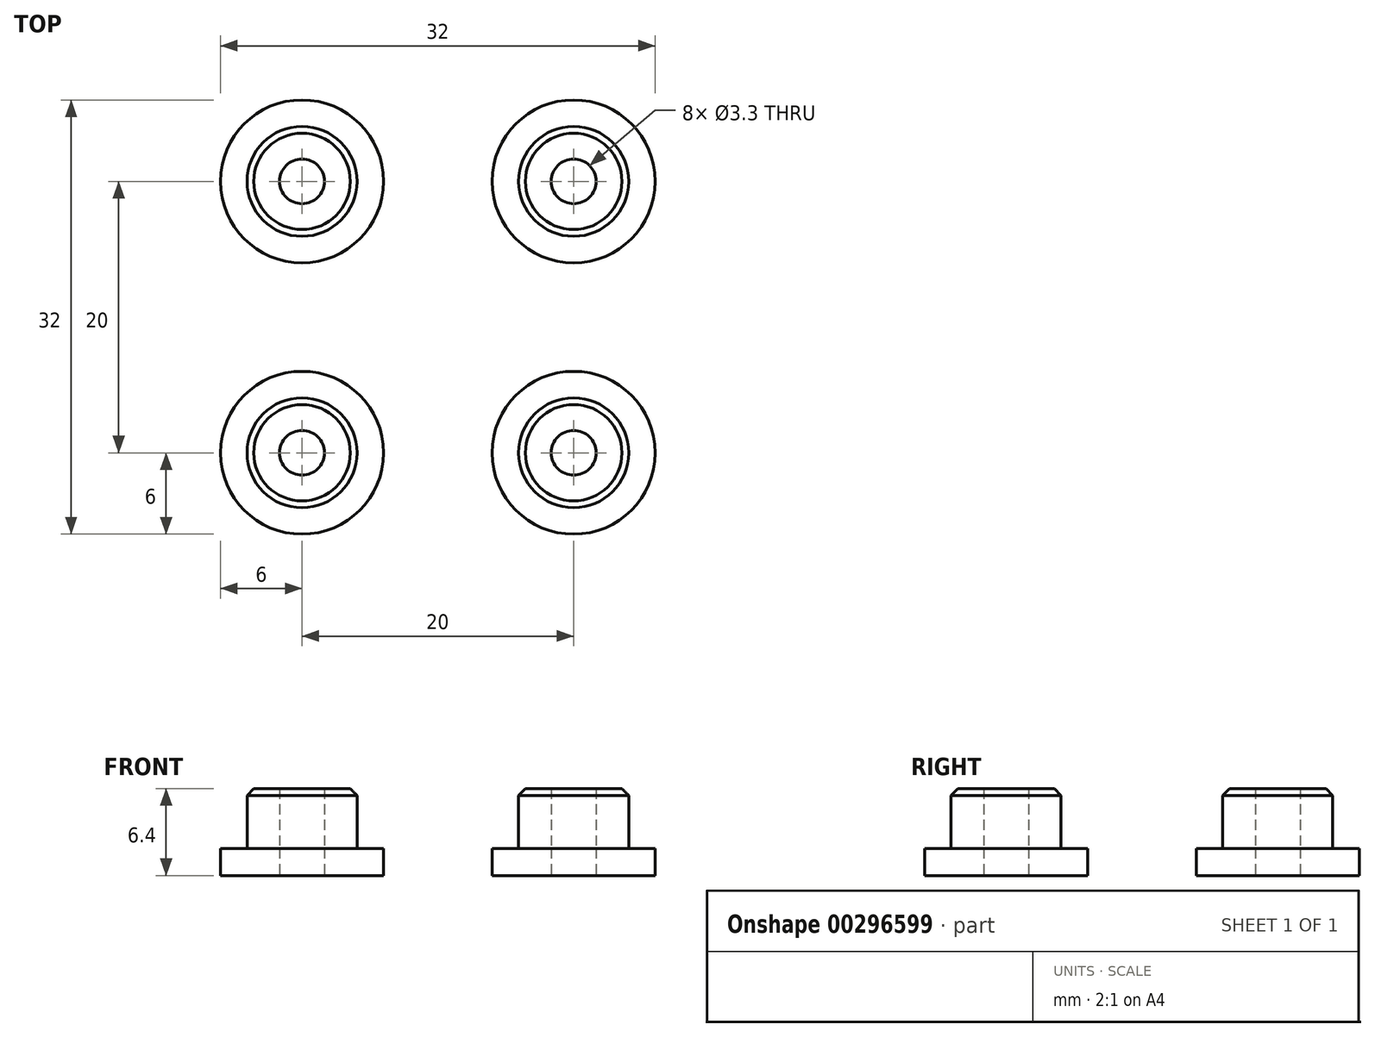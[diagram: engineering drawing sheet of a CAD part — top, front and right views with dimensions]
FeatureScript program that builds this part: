
annotation { "Feature Type Name" : "Feature", "Feature Type Description" : "" }
export const myFeature = defineFeature(function(context is Context, id is Id, definition is map)
    precondition{}
    {
        {
            var Q0;
            Q0=qCreatedBy(makeId("Top.planeOp"),FACE);
            var sketch = newSketch(context, id + "F0", { "sketchPlane" : qUnion([Q0])});
            skLineSegment(sketch, "E0.bottom", {"start": v(10, -10) * mm, "end": v(-10, -10) * mm, "construction": true});
            skLineSegment(sketch, "E0.top", {"start": v(10, 10) * mm, "end": v(-10, 10) * mm, "construction": true});
            skLineSegment(sketch, "E0.left", {"start": v(10, -10) * mm, "end": v(10, 10) * mm, "construction": true});
            skLineSegment(sketch, "E0.right", {"start": v(-10, -10) * mm, "end": v(-10, 10) * mm, "construction": true});
            skPoint(sketch, "E0.middle", {"position": v(0, 0) * mm});
            skCircle(sketch, "E1", {"center": v(-10, 10) * mm, "radius": 1.65 * mm});
            skCircle(sketch, "E2", {"center": v(-10, 10) * mm, "radius": 6 * mm});
            skCircle(sketch, "E3", {"center": v(10, 10) * mm, "radius": 1.65 * mm});
            skCircle(sketch, "E4", {"center": v(10, 10) * mm, "radius": 6 * mm});
            skCircle(sketch, "E5", {"center": v(10, -10) * mm, "radius": 1.65 * mm});
            skCircle(sketch, "E6", {"center": v(10, -10) * mm, "radius": 6 * mm});
            skCircle(sketch, "E7", {"center": v(-10, -10) * mm, "radius": 1.65 * mm});
            skCircle(sketch, "E8", {"center": v(-10, -10) * mm, "radius": 6 * mm});
            skSolve(sketch);
        }
        {
            var Q0;
            Q0 = qSketchRegion(id + "F0", true);
            extrude(context, id + "F1", {"entities" : qUnion([Q0]), "depth" : 2 * mm});
        }
        {
            var Q0;
            Q0=makeQuery(id+"F1.opExtrude","CAP_FACE",FACE,{"disambiguationData":[OSD([sQuery(id+"F0.wireOp",EDGE,"E7"),sQuery(id+"F0.wireOp",EDGE,"E8")])],"isStart":false});
            var sketch = newSketch(context, id + "F2", { "sketchPlane" : qUnion([Q0])});
            skLineSegment(sketch, "E9.bottom", {"start": v(10, 10) * mm, "end": v(-10, 10) * mm, "construction": true});
            skLineSegment(sketch, "E9.top", {"start": v(10, -10) * mm, "end": v(-10, -10) * mm, "construction": true});
            skLineSegment(sketch, "E9.left", {"start": v(10, 10) * mm, "end": v(10, -10) * mm, "construction": true});
            skLineSegment(sketch, "E9.right", {"start": v(-10, 10) * mm, "end": v(-10, -10) * mm, "construction": true});
            skPoint(sketch, "E9.middle", {"position": v(0, 0) * mm});
            skCircle(sketch, "E10", {"center": v(-10, 10) * mm, "radius": 1.65 * mm});
            skCircle(sketch, "E11", {"center": v(-10, 10) * mm, "radius": 4.05 * mm});
            skCircle(sketch, "E12", {"center": v(10, 10) * mm, "radius": 4.05 * mm});
            skCircle(sketch, "E13", {"center": v(10, 10) * mm, "radius": 1.65 * mm});
            skCircle(sketch, "E14", {"center": v(10, -10) * mm, "radius": 4.05 * mm});
            skCircle(sketch, "E15", {"center": v(10, -10) * mm, "radius": 1.65 * mm});
            skCircle(sketch, "E16", {"center": v(-10, -10) * mm, "radius": 1.65 * mm});
            skCircle(sketch, "E17", {"center": v(-10, -10) * mm, "radius": 4.05 * mm});
            skSolve(sketch);
        }
        {
            var Q0;
            Q0 = qSketchRegion(id + "F2", true);
            extrude(context, id + "F3", {"entities" : qUnion([Q0]), "depth" : 4.4 * mm});
        }
        {
            var Q0;
            Q0=makeQuery(id+"F3.opExtrude","CAP_EDGE",EDGE,{"disambiguationData":[OSD([sQuery(id+"F2.wireOp",EDGE,"E14")])],"isStart":false});
            var Q1;
            Q1=makeQuery(id+"F3.opExtrude","CAP_EDGE",EDGE,{"disambiguationData":[OSD([sQuery(id+"F2.wireOp",EDGE,"E12")])],"isStart":false});
            var Q2;
            Q2=makeQuery(id+"F3.opExtrude","CAP_EDGE",EDGE,{"disambiguationData":[OSD([sQuery(id+"F2.wireOp",EDGE,"E11")])],"isStart":false});
            var Q3;
            Q3=makeQuery(id+"F3.opExtrude","CAP_EDGE",EDGE,{"disambiguationData":[OSD([sQuery(id+"F2.wireOp",EDGE,"E17")])],"isStart":false});
            chamfer(context, id + "F4", {"entities" : qUnion([Q0, Q1, Q2, Q3]), "width" : 0.5 * mm, "tangentPropagation" : true});
        }
    });
